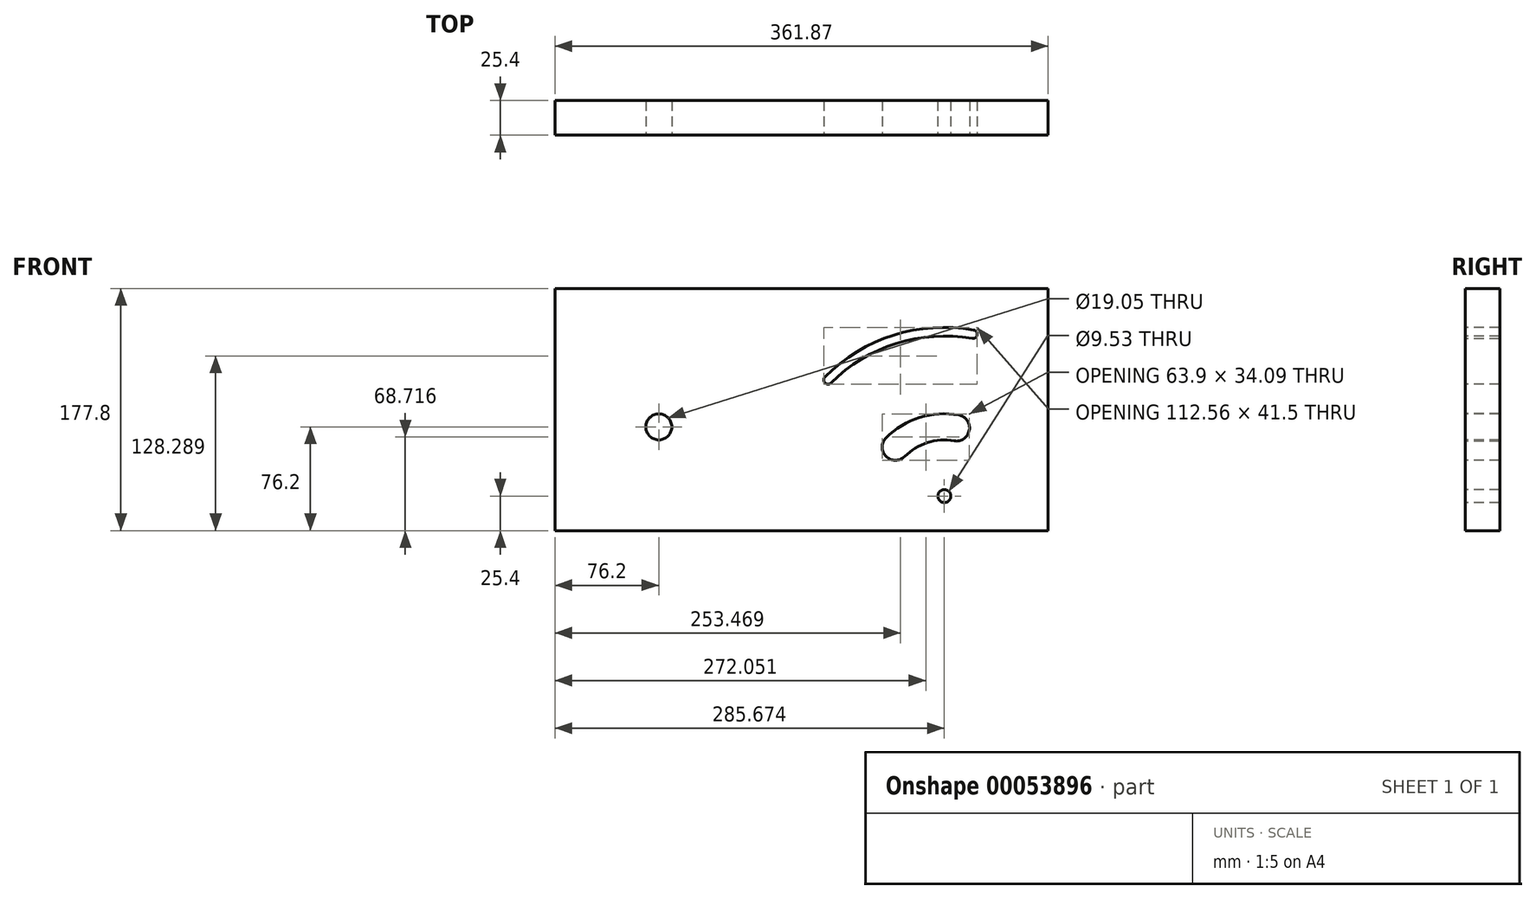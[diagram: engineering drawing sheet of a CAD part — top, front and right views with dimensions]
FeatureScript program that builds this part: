
annotation { "Feature Type Name" : "Feature", "Feature Type Description" : "" }
export const myFeature = defineFeature(function(context is Context, id is Id, definition is map)
    precondition{}
    {
        {
            var Q0;
            Q0=qCreatedBy(makeId("Front.planeOp"),FACE);
            var sketch = newSketch(context, id + "F0", { "sketchPlane" : qUnion([Q0])});
            skArc(sketch, "E0", {"start": v(-28.1, 25.72) * mm, "mid": v(-30.82, 22.4) * mm, "end": v(-33.15, 18.78) * mm});
            skCircle(sketch, "E1", {"center": v(0, 0) * mm, "radius": 9.53 * mm});
            skArc(sketch, "E2", {"start": v(5.87, 47.26) * mm, "mid": v(0, 47.63) * mm, "end": v(-5.87, 47.26) * mm});
            skLineSegment(sketch, "E3", {"start": v(-5.87, 47.26) * mm, "end": v(-7.62, 37.33) * mm});
            skLineSegment(sketch, "E4", {"start": v(5.87, 47.26) * mm, "end": v(7.62, 37.33) * mm});
            skLineSegment(sketch, "E5", {"start": v(7.62, 37.33) * mm, "end": v(-7.62, 37.33) * mm, "construction": true});
            skLineSegment(sketch, "E6", {"start": v(0, 47.63) * mm, "end": v(0, 37.33) * mm, "construction": true});
            skPoint(sketch, "E6.startSnap0", {"position": v(0, 47.63) * mm});
            skLineSegment(sketch, "E7.1.0", {"start": v(-32.53, 34.79) * mm, "end": v(-28.1, 25.72) * mm});
            skArc(sketch, "E7.1.1", {"start": v(-23.03, 41.69) * mm, "mid": v(-28, 38.53) * mm, "end": v(-32.53, 34.79) * mm});
            skLineSegment(sketch, "E7.1.2", {"start": v(-23.03, 41.69) * mm, "end": v(-15.78, 34.68) * mm});
            skLineSegment(sketch, "E7.2.0", {"start": v(-46.76, 9.02) * mm, "end": v(-37.86, 4.29) * mm});
            skArc(sketch, "E7.2.1", {"start": v(-43.14, 20.19) * mm, "mid": v(-45.3, 14.72) * mm, "end": v(-46.76, 9.02) * mm});
            skLineSegment(sketch, "E7.2.2", {"start": v(-43.14, 20.19) * mm, "end": v(-33.15, 18.78) * mm});
            skLineSegment(sketch, "E7.3.0", {"start": v(-43.14, -20.19) * mm, "end": v(-33.15, -18.78) * mm});
            skArc(sketch, "E7.3.1", {"start": v(-46.76, -9.02) * mm, "mid": v(-45.3, -14.72) * mm, "end": v(-43.14, -20.19) * mm});
            skLineSegment(sketch, "E7.3.2", {"start": v(-46.76, -9.02) * mm, "end": v(-37.86, -4.29) * mm});
            skLineSegment(sketch, "E7.4.0", {"start": v(-23.03, -41.69) * mm, "end": v(-15.78, -34.68) * mm});
            skArc(sketch, "E7.4.1", {"start": v(-32.53, -34.79) * mm, "mid": v(-28, -38.53) * mm, "end": v(-23.03, -41.69) * mm});
            skLineSegment(sketch, "E7.4.2", {"start": v(-32.53, -34.79) * mm, "end": v(-28.1, -25.72) * mm});
            skLineSegment(sketch, "E7.5.0", {"start": v(5.87, -47.26) * mm, "end": v(7.62, -37.33) * mm});
            skArc(sketch, "E7.5.1", {"start": v(-5.87, -47.26) * mm, "mid": v(0, -47.63) * mm, "end": v(5.87, -47.26) * mm});
            skLineSegment(sketch, "E7.5.2", {"start": v(-5.87, -47.26) * mm, "end": v(-7.62, -37.33) * mm});
            skLineSegment(sketch, "E7.6.0", {"start": v(32.53, -34.79) * mm, "end": v(28.1, -25.72) * mm});
            skArc(sketch, "E7.6.1", {"start": v(23.03, -41.69) * mm, "mid": v(28, -38.53) * mm, "end": v(32.53, -34.79) * mm});
            skLineSegment(sketch, "E7.6.2", {"start": v(23.03, -41.69) * mm, "end": v(15.78, -34.68) * mm});
            skLineSegment(sketch, "E7.7.0", {"start": v(46.76, -9.02) * mm, "end": v(37.86, -4.29) * mm});
            skArc(sketch, "E7.7.1", {"start": v(43.14, -20.19) * mm, "mid": v(45.3, -14.72) * mm, "end": v(46.76, -9.02) * mm});
            skLineSegment(sketch, "E7.7.2", {"start": v(43.14, -20.19) * mm, "end": v(33.15, -18.78) * mm});
            skLineSegment(sketch, "E7.8.0", {"start": v(43.14, 20.19) * mm, "end": v(33.15, 18.78) * mm});
            skArc(sketch, "E7.8.1", {"start": v(46.76, 9.02) * mm, "mid": v(45.3, 14.72) * mm, "end": v(43.14, 20.19) * mm});
            skLineSegment(sketch, "E7.8.2", {"start": v(46.76, 9.02) * mm, "end": v(37.86, 4.29) * mm});
            skLineSegment(sketch, "E7.9.0", {"start": v(23.03, 41.69) * mm, "end": v(15.78, 34.68) * mm});
            skArc(sketch, "E7.9.1", {"start": v(32.53, 34.79) * mm, "mid": v(28, 38.53) * mm, "end": v(23.03, 41.69) * mm});
            skLineSegment(sketch, "E7.9.2", {"start": v(32.53, 34.79) * mm, "end": v(28.1, 25.72) * mm});
            skArc(sketch, "E8.trimOffspring", {"start": v(-37.86, 4.29) * mm, "mid": v(-38.1, 0) * mm, "end": v(-37.86, -4.29) * mm});
            skArc(sketch, "E9.trimOffspring", {"start": v(-33.15, -18.78) * mm, "mid": v(-30.82, -22.4) * mm, "end": v(-28.1, -25.72) * mm});
            skArc(sketch, "E10.trimOffspring", {"start": v(-15.78, -34.68) * mm, "mid": v(-11.77, -36.24) * mm, "end": v(-7.62, -37.33) * mm});
            skArc(sketch, "E11.trimOffspring", {"start": v(7.62, -37.33) * mm, "mid": v(11.77, -36.24) * mm, "end": v(15.78, -34.68) * mm});
            skArc(sketch, "E12.trimOffspring", {"start": v(28.1, -25.72) * mm, "mid": v(30.82, -22.4) * mm, "end": v(33.15, -18.78) * mm});
            skArc(sketch, "E13.trimOffspring", {"start": v(37.86, -4.29) * mm, "mid": v(38.1, 0) * mm, "end": v(37.86, 4.29) * mm});
            skArc(sketch, "E14.trimOffspring", {"start": v(33.15, 18.78) * mm, "mid": v(30.82, 22.4) * mm, "end": v(28.1, 25.72) * mm});
            skArc(sketch, "E15.trimOffspring", {"start": v(15.78, 34.68) * mm, "mid": v(11.77, 36.24) * mm, "end": v(7.62, 37.33) * mm});
            skArc(sketch, "E16.trimOffspring", {"start": v(-7.62, 37.33) * mm, "mid": v(-11.77, 36.24) * mm, "end": v(-15.78, 34.68) * mm});
            skCircle(sketch, "E17", {"center": v(0, 0) * mm, "radius": 25.4 * mm, "construction": true});
            skLineSegment(sketch, "E18", {"start": v(0, 9.53) * mm, "end": v(0, 25.4) * mm, "construction": true});
            skLineSegment(sketch, "E19", {"start": v(0, 9.53) * mm, "end": v(0, 0) * mm, "construction": true});
            skCircle(sketch, "E20", {"center": v(0, 0) * mm, "radius": 15.88 * mm, "construction": true});
            skPoint(sketch, "E21", {"position": v(0, 15.88) * mm});
            skLineSegment(sketch, "E22", {"start": v(3.97, 25.09) * mm, "end": v(3.97, 8.66) * mm, "construction": true});
            skLineSegment(sketch, "E23", {"start": v(-3.97, 25.09) * mm, "end": v(-3.97, 8.66) * mm, "construction": true});
            skLineSegment(sketch, "E24", {"start": v(-3.97, 8.66) * mm, "end": v(3.97, 8.66) * mm, "construction": true});
            skLineSegment(sketch, "E25.1.0", {"start": v(-23.71, -9.1) * mm, "end": v(-9.48, -0.9) * mm, "construction": true});
            skLineSegment(sketch, "E25.1.1", {"start": v(-5.51, -7.77) * mm, "end": v(-9.48, -0.9) * mm, "construction": true});
            skLineSegment(sketch, "E25.1.2", {"start": v(-19.74, -15.98) * mm, "end": v(-5.51, -7.77) * mm, "construction": true});
            skLineSegment(sketch, "E25.1.3", {"start": v(-7.5, -4.33) * mm, "end": v(-22, -12.7) * mm, "construction": true});
            skLineSegment(sketch, "E25.2.0", {"start": v(19.74, -15.98) * mm, "end": v(5.51, -7.77) * mm, "construction": true});
            skLineSegment(sketch, "E25.2.1", {"start": v(9.48, -0.9) * mm, "end": v(5.51, -7.77) * mm, "construction": true});
            skLineSegment(sketch, "E25.2.2", {"start": v(23.71, -9.1) * mm, "end": v(9.48, -0.9) * mm, "construction": true});
            skLineSegment(sketch, "E25.2.3", {"start": v(7.5, -4.33) * mm, "end": v(22, -12.7) * mm, "construction": true});
            skPoint(sketch, "E26.orphan", {"position": v(8.25, -4.76) * mm});
            skPoint(sketch, "E27.orphan", {"position": v(-8.25, -4.76) * mm});
            skPoint(sketch, "E28.orphan", {"position": v(-3.97, 15.37) * mm});
            skPoint(sketch, "E29.orphan", {"position": v(3.97, 15.37) * mm});
            skPoint(sketch, "E30.orphan", {"position": v(15.3, -4.25) * mm});
            skPoint(sketch, "E31.orphan", {"position": v(11.33, -11.12) * mm});
            skPoint(sketch, "E32.orphan", {"position": v(-15.3, -4.25) * mm});
            skPoint(sketch, "E33.orphan", {"position": v(-11.33, -11.12) * mm});
            skSolve(sketch);
        }
        {
            var Q0;
            Q0=qCreatedBy(makeId("Front.planeOp"),FACE);
            var sketch = newSketch(context, id + "F1", { "sketchPlane" : qUnion([Q0])});
            skLineSegment(sketch, "E34", {"start": v(0, 0) * mm, "end": v(209.47, 0) * mm, "construction": true});
            skLineSegment(sketch, "E35", {"start": v(209.47, 0) * mm, "end": v(209.47, -50.8) * mm, "construction": true});
            skArc(sketch, "E36", {"start": v(173.55, -14.88) * mm, "mid": v(194.2, -2.35) * mm, "end": v(218.3, -0.77) * mm, "construction": true});
            skLineSegment(sketch, "E37", {"start": v(209.47, -50.8) * mm, "end": v(173.55, -14.88) * mm, "construction": true});
            skLineSegment(sketch, "E38", {"start": v(209.47, -50.8) * mm, "end": v(218.3, -0.77) * mm, "construction": true});
            skArc(sketch, "E39.0.startCap", {"start": v(180.38, -21.7) * mm, "mid": v(166.73, -21.7) * mm, "end": v(166.73, -8.05) * mm});
            skArc(sketch, "E39.0.endCap", {"start": v(219.97, 8.73) * mm, "mid": v(227.8, -2.45) * mm, "end": v(216.62, -10.28) * mm});
            skArc(sketch, "E39.0.left", {"start": v(166.73, -8.05) * mm, "mid": v(191.3, 6.85) * mm, "end": v(219.97, 8.73) * mm});
            skArc(sketch, "E39.0.right", {"start": v(180.38, -21.7) * mm, "mid": v(197.1, -11.56) * mm, "end": v(216.62, -10.28) * mm});
            skLineSegment(sketch, "E40.bottom", {"start": v(-76.2, 101.6) * mm, "end": v(285.67, 101.6) * mm});
            skLineSegment(sketch, "E40.top", {"start": v(-76.2, -76.2) * mm, "end": v(285.67, -76.2) * mm});
            skLineSegment(sketch, "E40.left", {"start": v(-76.2, 101.6) * mm, "end": v(-76.2, -76.2) * mm});
            skLineSegment(sketch, "E40.right", {"start": v(285.67, 101.6) * mm, "end": v(285.67, -76.2) * mm});
            skLineSegment(sketch, "E41", {"start": v(0, 0) * mm, "end": v(-76.2, 0) * mm, "construction": true});
            skLineSegment(sketch, "E42", {"start": v(209.47, 0) * mm, "end": v(285.67, -0.77) * mm, "construction": true});
            skCircle(sketch, "E43.0", {"center": v(0, 0) * mm, "radius": 9.53 * mm});
            skCircle(sketch, "E44", {"center": v(209.47, -50.8) * mm, "radius": 4.76 * mm});
            skArc(sketch, "E45", {"start": v(124.16, 34.51) * mm, "mid": v(173.2, 64.27) * mm, "end": v(230.42, 68.02) * mm, "construction": true});
            skLineSegment(sketch, "E46", {"start": v(209.47, 0) * mm, "end": v(209.47, 69.85) * mm, "construction": true});
            skArc(sketch, "E47.0.startCap", {"start": v(126.4, 32.27) * mm, "mid": v(121.92, 32.27) * mm, "end": v(121.92, 36.76) * mm});
            skArc(sketch, "E47.0.endCap", {"start": v(230.98, 71.14) * mm, "mid": v(233.55, 67.47) * mm, "end": v(229.87, 64.9) * mm});
            skArc(sketch, "E47.0.left", {"start": v(121.92, 36.76) * mm, "mid": v(172.24, 67.3) * mm, "end": v(230.98, 71.14) * mm});
            skArc(sketch, "E47.0.right", {"start": v(126.4, 32.27) * mm, "mid": v(174.15, 61.24) * mm, "end": v(229.87, 64.9) * mm});
            skSolve(sketch);
        }
        {
            var Q0;
            Q0 = qSketchRegion(id + "F1", true);
            extrude(context, id + "F2", {"entities" : qUnion([Q0]), "oppositeDirection" : true, "depth" : 25.4 * mm});
        }
    });
